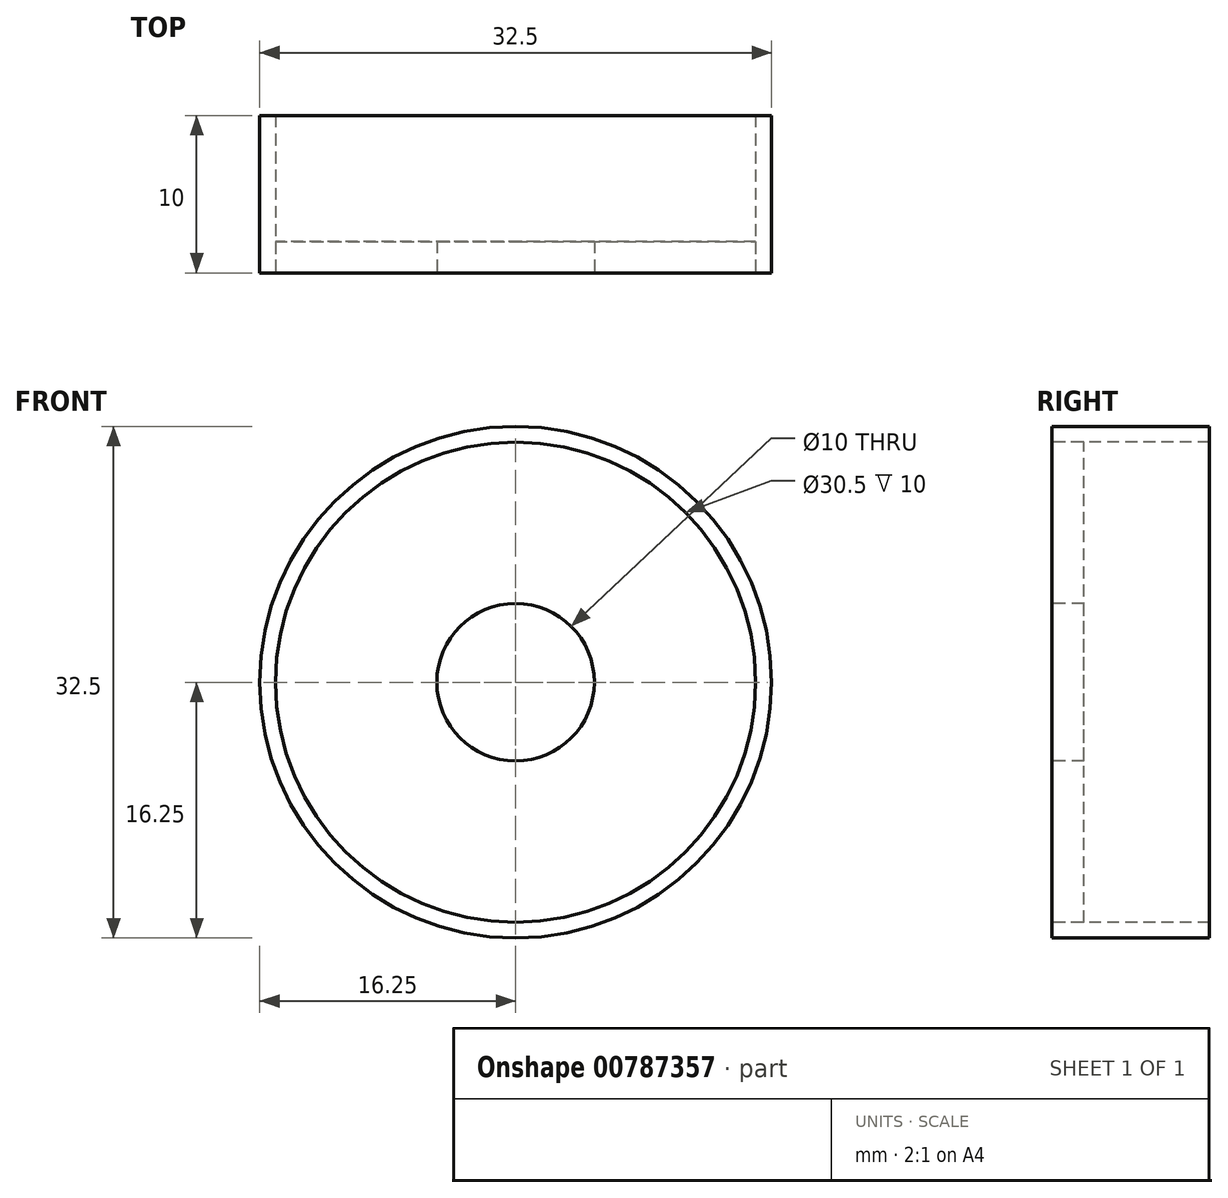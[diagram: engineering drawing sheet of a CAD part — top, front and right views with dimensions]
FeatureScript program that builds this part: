
annotation { "Feature Type Name" : "Feature", "Feature Type Description" : "" }
export const myFeature = defineFeature(function(context is Context, id is Id, definition is map)
    precondition{}
    {
        {
            var Q0;
            Q0=qCreatedBy(makeId("Front.planeOp"),FACE);
            var sketch = newSketch(context, id + "F0", { "sketchPlane" : qUnion([Q0])});
            skCircle(sketch, "E0", {"center": v(0, 0) * mm, "radius": 15.25 * mm});
            skCircle(sketch, "E1", {"center": v(0, 0) * mm, "radius": 16.25 * mm});
            skSolve(sketch);
        }
        {
            var Q0;
            Q0=makeQuery(id+"F0.imprint","IMPRINT",FACE,{"disambiguationData":[TD([[makeQuery(id+"F0.imprint","IMPRINT",EDGE,{"derivedFrom":sQuery(id+"F0.wireOp",EDGE,"E1")}),1.0]])]});
            extrude(context, id + "F1", {"entities" : qUnion([Q0]), "oppositeDirection" : true, "depth" : 10 * mm, "offsetDistance" : 25 * mm});
        }
        {
            var Q0;
            Q0=qCreatedBy(makeId("Front.planeOp"),FACE);
            var sketch = newSketch(context, id + "F2", { "sketchPlane" : qUnion([Q0])});
            skCircle(sketch, "E2", {"center": v(0, 0) * mm, "radius": 15.25 * mm});
            skCircle(sketch, "E3", {"center": v(0, 0) * mm, "radius": 5 * mm});
            skSolve(sketch);
        }
        {
            var Q0;
            Q0=qSketchRegion(id+"F2",true);
            extrude(context, id + "F3", {"entities" : qUnion([Q0]), "operationType" : NewBodyOperationType.REMOVE, "depth" : 8 * mm, "offsetDistance" : 25 * mm});
        }
        {
            var Q0;
            Q0=qSketchRegion(id+"F2",true);
            extrude(context, id + "F4", {"entities" : qUnion([Q0]), "oppositeDirection" : true, "depth" : 2 * mm, "offsetDistance" : 25 * mm});
        }
    });
